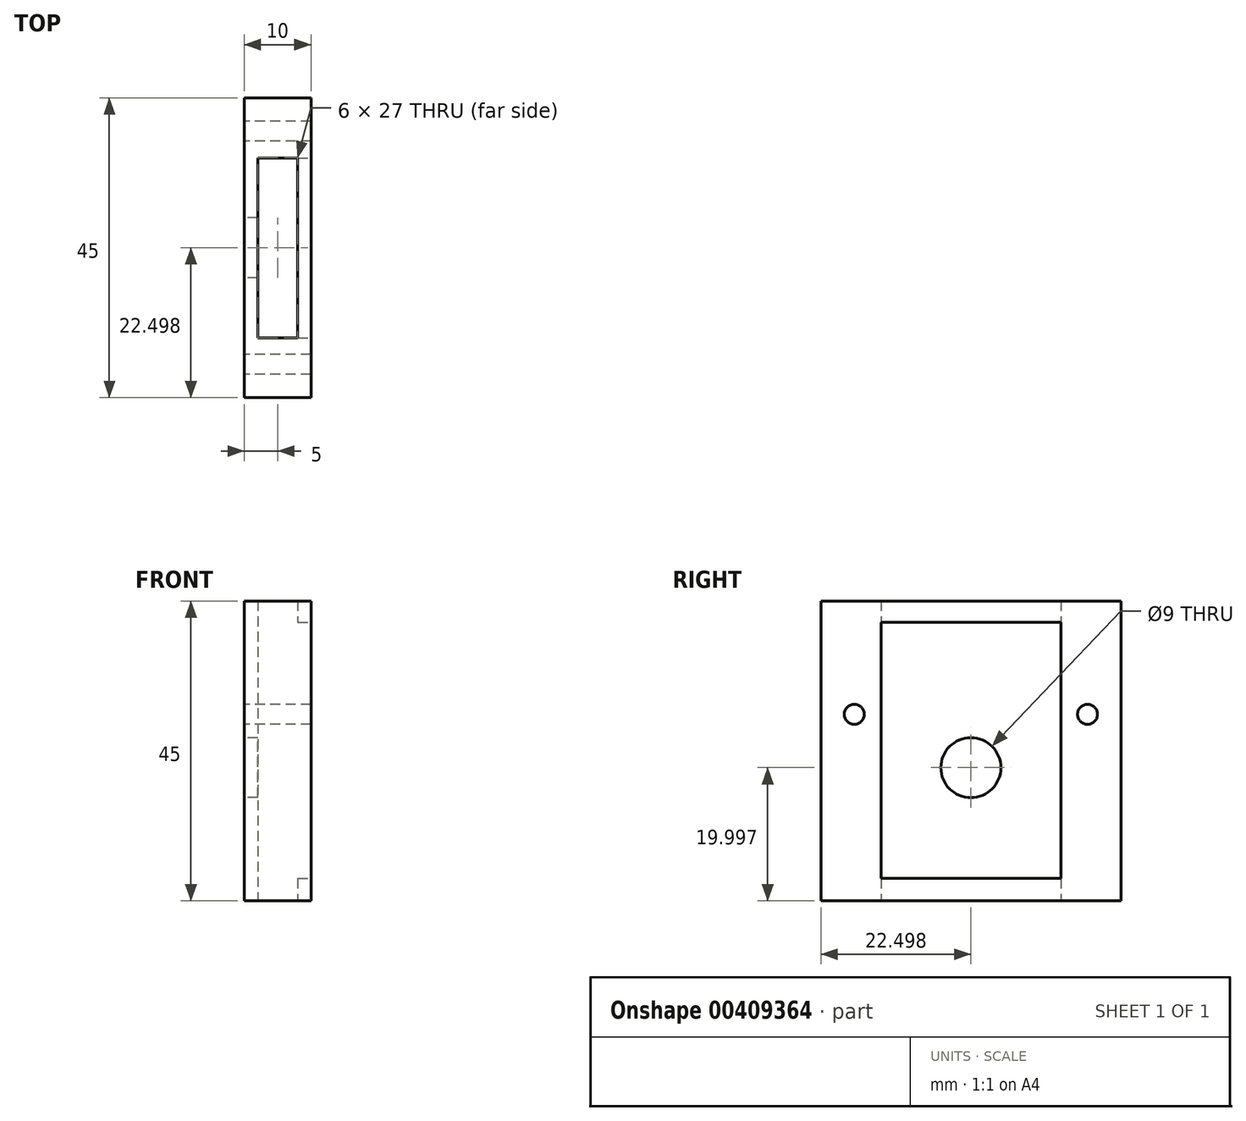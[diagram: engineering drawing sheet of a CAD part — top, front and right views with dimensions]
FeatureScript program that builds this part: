
annotation { "Feature Type Name" : "Feature", "Feature Type Description" : "" }
export const myFeature = defineFeature(function(context is Context, id is Id, definition is map)
    precondition{}
    {
        {
            var Q0;
            Q0=qCreatedBy(makeId("Right.planeOp"),FACE);
            var sketch = newSketch(context, id + "F0", { "sketchPlane" : qUnion([Q0])});
            skLineSegment(sketch, "E0.bottom", {"start": v(0, 45.3) * mm, "end": v(45, 45.3) * mm});
            skLineSegment(sketch, "E0.top", {"start": v(0, 0.3) * mm, "end": v(45, 0.3) * mm});
            skLineSegment(sketch, "E0.left", {"start": v(0, 45.3) * mm, "end": v(0, 0.3) * mm});
            skLineSegment(sketch, "E0.right", {"start": v(45, 45.3) * mm, "end": v(45, 0.3) * mm});
            skSolve(sketch);
        }
        {
            var Q0;
            Q0=makeQuery(id+"F0.imprint","IMPRINT",FACE,{"disambiguationData":[TD([[makeQuery(id+"F0.imprint","IMPRINT",EDGE,{"derivedFrom":sQuery(id+"F0.wireOp",EDGE,"E0.bottom")}),-1.0]])]});
            extrude(context, id + "F1", {"entities" : qUnion([Q0]), "depth" : 10 * mm, "offsetDistance" : 25 * mm});
        }
        {
            var Q0;
            Q0=qCreatedBy(makeId("Top.planeOp"),FACE);
            var sketch = newSketch(context, id + "F2", { "sketchPlane" : qUnion([Q0])});
            skLineSegment(sketch, "E1.bottom", {"start": v(2, 36) * mm, "end": v(8, 36) * mm});
            skLineSegment(sketch, "E1.top", {"start": v(2, 9) * mm, "end": v(8, 9) * mm});
            skLineSegment(sketch, "E1.left", {"start": v(2, 36) * mm, "end": v(2, 9) * mm});
            skLineSegment(sketch, "E1.right", {"start": v(8, 36) * mm, "end": v(8, 9) * mm});
            skSolve(sketch);
        }
        {
            var Q0;
            Q0 = qSketchRegion(id + "F2", true);
            extrude(context, id + "F3", {"entities" : qUnion([Q0]), "operationType" : NewBodyOperationType.REMOVE, "depth" : 4510 * mm, "offsetDistance" : 25 * mm});
        }
        {
            var Q0;
            Q0=qCreatedBy(makeId("Right.planeOp"),FACE);
            var sketch = newSketch(context, id + "F4", { "sketchPlane" : qUnion([Q0])});
            skCircle(sketch, "E2", {"center": v(22.5, 20.3) * mm, "radius": 4.5 * mm});
            skCircle(sketch, "E3", {"center": v(5, 28.3) * mm, "radius": 1.5 * mm});
            skCircle(sketch, "E4", {"center": v(40, 28.3) * mm, "radius": 1.5 * mm});
            skSolve(sketch);
        }
        {
            var Q0;
            Q0 = qSketchRegion(id + "F4", true);
            extrude(context, id + "F5", {"entities" : qUnion([Q0]), "operationType" : NewBodyOperationType.REMOVE, "depth" : 10 * mm, "offsetDistance" : 25 * mm});
        }
        {
            var Q0;
            Q0=makeQuery(id+"F1.opExtrude","CAP_FACE",FACE,{"disambiguationData":[OSD([sQuery(id+"F0.wireOp",EDGE,"E0.bottom"),sQuery(id+"F0.wireOp",EDGE,"E0.top"),sQuery(id+"F0.wireOp",EDGE,"E0.left"),sQuery(id+"F0.wireOp",EDGE,"E0.right")])],"isStart":false});
            var sketch = newSketch(context, id + "F6", { "sketchPlane" : qUnion([Q0])});
            skLineSegment(sketch, "E5.bottom", {"start": v(9, 3.68) * mm, "end": v(36, 3.68) * mm});
            skLineSegment(sketch, "E5.top", {"start": v(9, 42.14) * mm, "end": v(36, 42.14) * mm});
            skLineSegment(sketch, "E5.left", {"start": v(9, 3.68) * mm, "end": v(9, 42.14) * mm});
            skLineSegment(sketch, "E5.right", {"start": v(36, 3.68) * mm, "end": v(36, 42.14) * mm});
            skSolve(sketch);
        }
        {
            var Q0;
            Q0=makeQuery(id+"F6.imprint","IMPRINT",FACE,{"disambiguationData":[TD([[makeQuery(id+"F6.imprint","IMPRINT",EDGE,{"derivedFrom":sQuery(id+"F6.wireOp",EDGE,"E5.bottom")}),1.0]])]});
            extrude(context, id + "F7", {"entities" : qUnion([Q0]), "operationType" : NewBodyOperationType.REMOVE, "oppositeDirection" : true, "depth" : 5 * mm, "offsetDistance" : 25 * mm});
        }
    });
